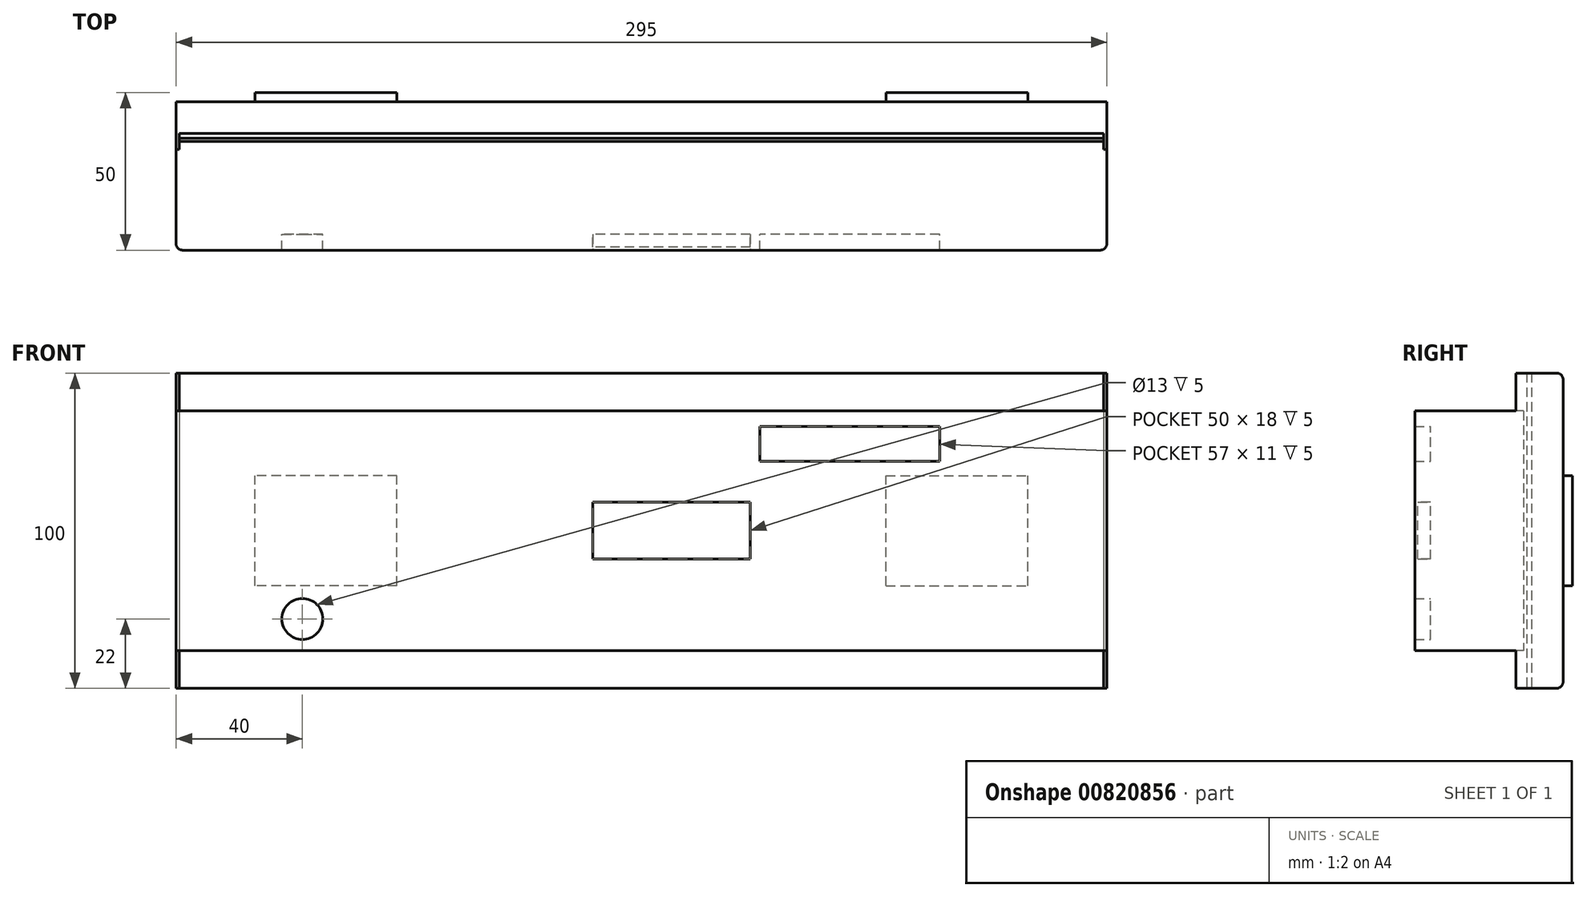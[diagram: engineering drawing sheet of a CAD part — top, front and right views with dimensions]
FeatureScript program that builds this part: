
annotation { "Feature Type Name" : "Feature", "Feature Type Description" : "" }
export const myFeature = defineFeature(function(context is Context, id is Id, definition is map)
    precondition{}
    {
        {
            var Q0;
            Q0=qCreatedBy(makeId("Front.planeOp"),FACE);
            var sketch = newSketch(context, id + "F0", { "sketchPlane" : qUnion([Q0])});
            skLineSegment(sketch, "E0.bottom", {"start": v(147.5, -50) * mm, "end": v(-147.5, -50) * mm});
            skLineSegment(sketch, "E0.top", {"start": v(147.5, 50) * mm, "end": v(-147.5, 50) * mm});
            skLineSegment(sketch, "E0.left", {"start": v(147.5, -50) * mm, "end": v(147.5, 50) * mm});
            skLineSegment(sketch, "E0.right", {"start": v(-147.5, -50) * mm, "end": v(-147.5, 50) * mm});
            skPoint(sketch, "E0.middle", {"position": v(0, 0) * mm});
            skSolve(sketch);
        }
        {
            var Q0;
            Q0 = qSketchRegion(id + "F0", true);
            extrude(context, id + "F1", {"entities" : qUnion([Q0]), "depth" : 47 * mm, "offsetDistance" : 25 * mm});
        }
        {
            var Q0;
            Q0=makeQuery(id+"F1.opExtrude","CAP_FACE",FACE,{"disambiguationData":[OSD([sQuery(id+"F0.wireOp",EDGE,"E0.bottom"),sQuery(id+"F0.wireOp",EDGE,"E0.top"),sQuery(id+"F0.wireOp",EDGE,"E0.left"),sQuery(id+"F0.wireOp",EDGE,"E0.right")])],"isStart":false});
            var sketch = newSketch(context, id + "F2", { "sketchPlane" : qUnion([Q0])});
            skLineSegment(sketch, "E1.bottom", {"start": v(-147.5, -50) * mm, "end": v(147.5, -50) * mm});
            skLineSegment(sketch, "E1.top", {"start": v(-147.5, -38) * mm, "end": v(147.5, -38) * mm});
            skLineSegment(sketch, "E1.left", {"start": v(-147.5, -50) * mm, "end": v(-147.5, -38) * mm});
            skLineSegment(sketch, "E1.right", {"start": v(147.5, -50) * mm, "end": v(147.5, -38) * mm});
            skLineSegment(sketch, "E2.bottom", {"start": v(147.5, 50) * mm, "end": v(-147.5, 50) * mm});
            skLineSegment(sketch, "E2.top", {"start": v(147.5, 38) * mm, "end": v(-147.5, 38) * mm});
            skLineSegment(sketch, "E2.left", {"start": v(147.5, 50) * mm, "end": v(147.5, 38) * mm});
            skLineSegment(sketch, "E2.right", {"start": v(-147.5, 50) * mm, "end": v(-147.5, 38) * mm});
            skSolve(sketch);
        }
        {
            var Q0;
            Q0 = qSketchRegion(id + "F2", true);
            extrude(context, id + "F3", {"entities" : qUnion([Q0]), "operationType" : NewBodyOperationType.REMOVE, "oppositeDirection" : true, "depth" : (47 - 15) * mm, "offsetDistance" : 25 * mm});
        }
        {
            var Q0;
            Q0=makeQuery(id+"F3.boolean.opBoolean","COPY",FACE,{"derivedFrom":makeQuery(id+"F3.opExtrude","CAP_FACE",FACE,{"disambiguationData":[OSD([sQuery(id+"F2.wireOp",EDGE,"E2.bottom"),sQuery(id+"F2.wireOp",EDGE,"E2.top"),sQuery(id+"F2.wireOp",EDGE,"E2.left"),sQuery(id+"F2.wireOp",EDGE,"E2.right")])],"isStart":false})});
            var sketch = newSketch(context, id + "F4", { "sketchPlane" : qUnion([Q0])});
            skLineSegment(sketch, "E3.bottom", {"start": v(-146.5, 50) * mm, "end": v(146.5, 50) * mm});
            skLineSegment(sketch, "E3.top", {"start": v(-146.5, 38) * mm, "end": v(146.5, 38) * mm});
            skLineSegment(sketch, "E3.left", {"start": v(-146.5, 50) * mm, "end": v(-146.5, 38) * mm});
            skLineSegment(sketch, "E3.right", {"start": v(146.5, 50) * mm, "end": v(146.5, 38) * mm});
            skSolve(sketch);
        }
        {
            var Q0;
            Q0=makeQuery(id+"F3.boolean.opBoolean","COPY",FACE,{"derivedFrom":makeQuery(id+"F3.opExtrude","CAP_FACE",FACE,{"disambiguationData":[OSD([sQuery(id+"F2.wireOp",EDGE,"E1.bottom"),sQuery(id+"F2.wireOp",EDGE,"E1.top"),sQuery(id+"F2.wireOp",EDGE,"E1.left"),sQuery(id+"F2.wireOp",EDGE,"E1.right")])],"isStart":false})});
            var sketch = newSketch(context, id + "F5", { "sketchPlane" : qUnion([Q0])});
            skLineSegment(sketch, "E4.bottom", {"start": v(-146.5, -50) * mm, "end": v(146.5, -50) * mm});
            skLineSegment(sketch, "E4.top", {"start": v(-146.5, -38) * mm, "end": v(146.5, -38) * mm});
            skLineSegment(sketch, "E4.left", {"start": v(-146.5, -50) * mm, "end": v(-146.5, -38) * mm});
            skLineSegment(sketch, "E4.right", {"start": v(146.5, -50) * mm, "end": v(146.5, -38) * mm});
            skSolve(sketch);
        }
        {
            var Q0;
            Q0 = qSketchRegion(id + "F4", true);
            var Q1;
            Q1 = qSketchRegion(id + "F5", true);
            extrude(context, id + "F6", {"entities" : qUnion([Q0, Q1]), "operationType" : NewBodyOperationType.REMOVE, "oppositeDirection" : true, "depth" : 5 * mm, "offsetDistance" : 25 * mm});
        }
        {
            var Q0;
            Q0=makeQuery(id+"F6.boolean.opBoolean","MERGE",FACE,{"derivedFrom":[makeQuery(id+"F3.boolean.opBoolean","COPY",FACE,{"derivedFrom":makeQuery(id+"F3.opExtrude","SWEPT_FACE",FACE,{"disambiguationData":[OSD([sQuery(id+"F2.wireOp",EDGE,"E1.top")])]})}),makeQuery(id+"F6.opExtrude","SWEPT_FACE",FACE,{"disambiguationData":[OSD([sQuery(id+"F5.wireOp",EDGE,"E4.top")])]})]});
            var sketch = newSketch(context, id + "F7", { "sketchPlane" : qUnion([Q0])});
            skLineSegment(sketch, "E5.bottom", {"start": v(-146.5, 10) * mm, "end": v(146.5, 10) * mm});
            skLineSegment(sketch, "E5.top", {"start": v(-146.5, 12.5) * mm, "end": v(146.5, 12.5) * mm});
            skLineSegment(sketch, "E5.left", {"start": v(-146.5, 10) * mm, "end": v(-146.5, 12.5) * mm});
            skLineSegment(sketch, "E5.right", {"start": v(146.5, 10) * mm, "end": v(146.5, 12.5) * mm});
            skSolve(sketch);
        }
        {
            var Q0;
            Q0 = qSketchRegion(id + "F7", true);
            extrude(context, id + "F8", {"entities" : qUnion([Q0]), "operationType" : NewBodyOperationType.REMOVE, "endBound" : BoundingType.THROUGH_ALL, "oppositeDirection" : true, "depth" : 25 * mm, "offsetDistance" : 25 * mm});
        }
        {
            var Q0;
            Q0=makeQuery(id+"F1.opExtrude","CAP_FACE",FACE,{"disambiguationData":[OSD([sQuery(id+"F0.wireOp",EDGE,"E0.bottom"),sQuery(id+"F0.wireOp",EDGE,"E0.top"),sQuery(id+"F0.wireOp",EDGE,"E0.left"),sQuery(id+"F0.wireOp",EDGE,"E0.right")])],"isStart":false});
            var sketch = newSketch(context, id + "F9", { "sketchPlane" : qUnion([Q0])});
            skLineSegment(sketch, "E6.bottom", {"start": v(34.5, -9) * mm, "end": v(-15.5, -9) * mm});
            skLineSegment(sketch, "E6.top", {"start": v(34.5, 9) * mm, "end": v(-15.5, 9) * mm});
            skLineSegment(sketch, "E6.left", {"start": v(34.5, -9) * mm, "end": v(34.5, 9) * mm});
            skLineSegment(sketch, "E6.right", {"start": v(-15.5, -9) * mm, "end": v(-15.5, 9) * mm});
            skPoint(sketch, "E6.middle", {"position": v(9.5, 0) * mm});
            skCircle(sketch, "E7", {"center": v(-107.5, -28) * mm, "radius": 6.5 * mm});
            skLineSegment(sketch, "E8.bottom", {"start": v(94.5, 22) * mm, "end": v(37.5, 22) * mm});
            skLineSegment(sketch, "E8.top", {"start": v(94.5, 33) * mm, "end": v(37.5, 33) * mm});
            skLineSegment(sketch, "E8.left", {"start": v(94.5, 22) * mm, "end": v(94.5, 33) * mm});
            skLineSegment(sketch, "E8.right", {"start": v(37.5, 22) * mm, "end": v(37.5, 33) * mm});
            skPoint(sketch, "E8.middle", {"position": v(66, 27.5) * mm});
            skSolve(sketch);
        }
        {
            var Q0;
            Q0 = qSketchRegion(id + "F9", true);
            extrude(context, id + "F10", {"entities" : qUnion([Q0]), "operationType" : NewBodyOperationType.REMOVE, "oppositeDirection" : true, "depth" : 5 * mm, "offsetDistance" : 25 * mm});
        }
        {
            var Q0;
            Q0=makeQuery(id+"F10.boolean.opBoolean","COPY",FACE,{"derivedFrom":makeQuery(id+"F10.opExtrude","CAP_FACE",FACE,{"disambiguationData":[OSD([sQuery(id+"F9.wireOp",EDGE,"E6.bottom"),sQuery(id+"F9.wireOp",EDGE,"E6.top"),sQuery(id+"F9.wireOp",EDGE,"E6.left"),sQuery(id+"F9.wireOp",EDGE,"E6.right")])],"isStart":false})});
            extrude(context, id + "F11", {"entities" : qUnion([Q0]), "depth" : 4 * mm, "offsetDistance" : 25 * mm});
        }
        {
            var Q0;
            Q0=makeQuery(id+"F10.boolean.opBoolean","COPY",FACE,{"derivedFrom":makeQuery(id+"F10.opExtrude","CAP_FACE",FACE,{"disambiguationData":[OSD([sQuery(id+"F9.wireOp",EDGE,"E7")])],"isStart":false})});
            var Q1;
            Q1=makeQuery(id+"F10.boolean.opBoolean","COPY",FACE,{"derivedFrom":makeQuery(id+"F10.opExtrude","CAP_FACE",FACE,{"disambiguationData":[OSD([sQuery(id+"F9.wireOp",EDGE,"E8.bottom"),sQuery(id+"F9.wireOp",EDGE,"E8.top"),sQuery(id+"F9.wireOp",EDGE,"E8.left"),sQuery(id+"F9.wireOp",EDGE,"E8.right")])],"isStart":false})});
            var Q2;
            Q2=makeQuery(id+"F1.opExtrude","CAP_FACE",FACE,{"disambiguationData":[OSD([sQuery(id+"F0.wireOp",EDGE,"E0.bottom"),sQuery(id+"F0.wireOp",EDGE,"E0.top"),sQuery(id+"F0.wireOp",EDGE,"E0.left"),sQuery(id+"F0.wireOp",EDGE,"E0.right")])],"isStart":false});
            extrude(context, id + "F12", {"entities" : qUnion([Q0, Q1]), "endBound" : BoundingType.UP_TO_SURFACE, "depth" : 25 * mm, "endBoundEntityFace" : qUnion([Q2]), "offsetDistance" : 25 * mm});
        }
        {
            var Q0;
            Q0=makeQuery(id+"F8.boolean.opBoolean","MERGE",FACE,{"derivedFrom":[makeQuery(id+"F6.boolean.opBoolean","COPY",FACE,{"derivedFrom":makeQuery(id+"F6.opExtrude","CAP_FACE",FACE,{"disambiguationData":[OSD([sQuery(id+"F4.wireOp",EDGE,"E3.bottom"),sQuery(id+"F4.wireOp",EDGE,"E3.top"),sQuery(id+"F4.wireOp",EDGE,"E3.left"),sQuery(id+"F4.wireOp",EDGE,"E3.right")])],"isStart":false})}),makeQuery(id+"F6.boolean.opBoolean","COPY",FACE,{"derivedFrom":makeQuery(id+"F6.opExtrude","CAP_FACE",FACE,{"disambiguationData":[OSD([sQuery(id+"F5.wireOp",EDGE,"E4.bottom"),sQuery(id+"F5.wireOp",EDGE,"E4.top"),sQuery(id+"F5.wireOp",EDGE,"E4.left"),sQuery(id+"F5.wireOp",EDGE,"E4.right")])],"isStart":false})}),makeQuery(id+"F8.opExtrude","SWEPT_FACE",FACE,{"disambiguationData":[OSD([sQuery(id+"F7.wireOp",EDGE,"E5.bottom")])]})]});
            extrude(context, id + "F13", {"entities" : qUnion([Q0]), "depth" : 1.5 * mm, "offsetDistance" : 25 * mm});
        }
        {
            var Q0;
            Q0=makeQuery(id+"F1.opExtrude","CAP_FACE",FACE,{"disambiguationData":[OSD([sQuery(id+"F0.wireOp",EDGE,"E0.bottom"),sQuery(id+"F0.wireOp",EDGE,"E0.top"),sQuery(id+"F0.wireOp",EDGE,"E0.left"),sQuery(id+"F0.wireOp",EDGE,"E0.right")])],"isStart":true});
            var sketch = newSketch(context, id + "F14", { "sketchPlane" : qUnion([Q0])});
            skLineSegment(sketch, "E9.bottom", {"start": v(-77.5, -17.5) * mm, "end": v(-122.5, -17.5) * mm});
            skLineSegment(sketch, "E9.top", {"start": v(-77.5, 17.5) * mm, "end": v(-122.5, 17.5) * mm});
            skLineSegment(sketch, "E9.left", {"start": v(-77.5, -17.5) * mm, "end": v(-77.5, 17.5) * mm});
            skLineSegment(sketch, "E9.right", {"start": v(-122.5, -17.5) * mm, "end": v(-122.5, 17.5) * mm});
            skPoint(sketch, "E9.middle", {"position": v(-100, 0) * mm});
            skLineSegment(sketch, "E10.bottom", {"start": v(77.5, -17.5) * mm, "end": v(122.5, -17.5) * mm});
            skLineSegment(sketch, "E10.top", {"start": v(77.5, 17.5) * mm, "end": v(122.5, 17.5) * mm});
            skLineSegment(sketch, "E10.left", {"start": v(77.5, -17.5) * mm, "end": v(77.5, 17.5) * mm});
            skLineSegment(sketch, "E10.right", {"start": v(122.5, -17.5) * mm, "end": v(122.5, 17.5) * mm});
            skPoint(sketch, "E10.middle", {"position": v(100, 0) * mm});
            skSolve(sketch);
        }
        {
            var Q0;
            Q0 = qSketchRegion(id + "F14", true);
            extrude(context, id + "F15", {"entities" : qUnion([Q0]), "operationType" : NewBodyOperationType.ADD, "depth" : 3 * mm, "offsetDistance" : 25 * mm});
        }
        {
            var Q0;
            Q0=makeQuery(id+"F3.boolean.opBoolean","COPY",EDGE,{"derivedFrom":makeQuery(id+"F3.opExtrude","CAP_EDGE",EDGE,{"disambiguationData":[OSD([sQuery(id+"F2.wireOp",EDGE,"E2.top")])],"isStart":true})});
            var Q1;
            Q1=makeQuery(id+"F1.opExtrude","CAP_EDGE",EDGE,{"disambiguationData":[OSD([sQuery(id+"F0.wireOp",EDGE,"E0.left")])],"isStart":false});
            var Q2;
            Q2=makeQuery(id+"F1.opExtrude","CAP_EDGE",EDGE,{"disambiguationData":[OSD([sQuery(id+"F0.wireOp",EDGE,"E0.right")])],"isStart":false});
            var Q3;
            Q3=makeQuery(id+"F3.boolean.opBoolean","COPY",EDGE,{"derivedFrom":makeQuery(id+"F3.opExtrude","CAP_EDGE",EDGE,{"disambiguationData":[OSD([sQuery(id+"F2.wireOp",EDGE,"E1.top")])],"isStart":true})});
            var Q4;
            Q4=makeQuery(id+"F1.opExtrude","CAP_EDGE",EDGE,{"disambiguationData":[OSD([sQuery(id+"F0.wireOp",EDGE,"E0.top")])],"isStart":true});
            var Q5;
            Q5=makeQuery(id+"F1.opExtrude","CAP_EDGE",EDGE,{"disambiguationData":[OSD([sQuery(id+"F0.wireOp",EDGE,"E0.bottom")])],"isStart":true});
            fillet(context, id + "F16", {"entities" : qUnion([Q0, Q1, Q2, Q3, Q4, Q5]), "radius" : 2 * mm, "tangentPropagation" : true, "allowEdgeOverflow" : false});
        }
    });
